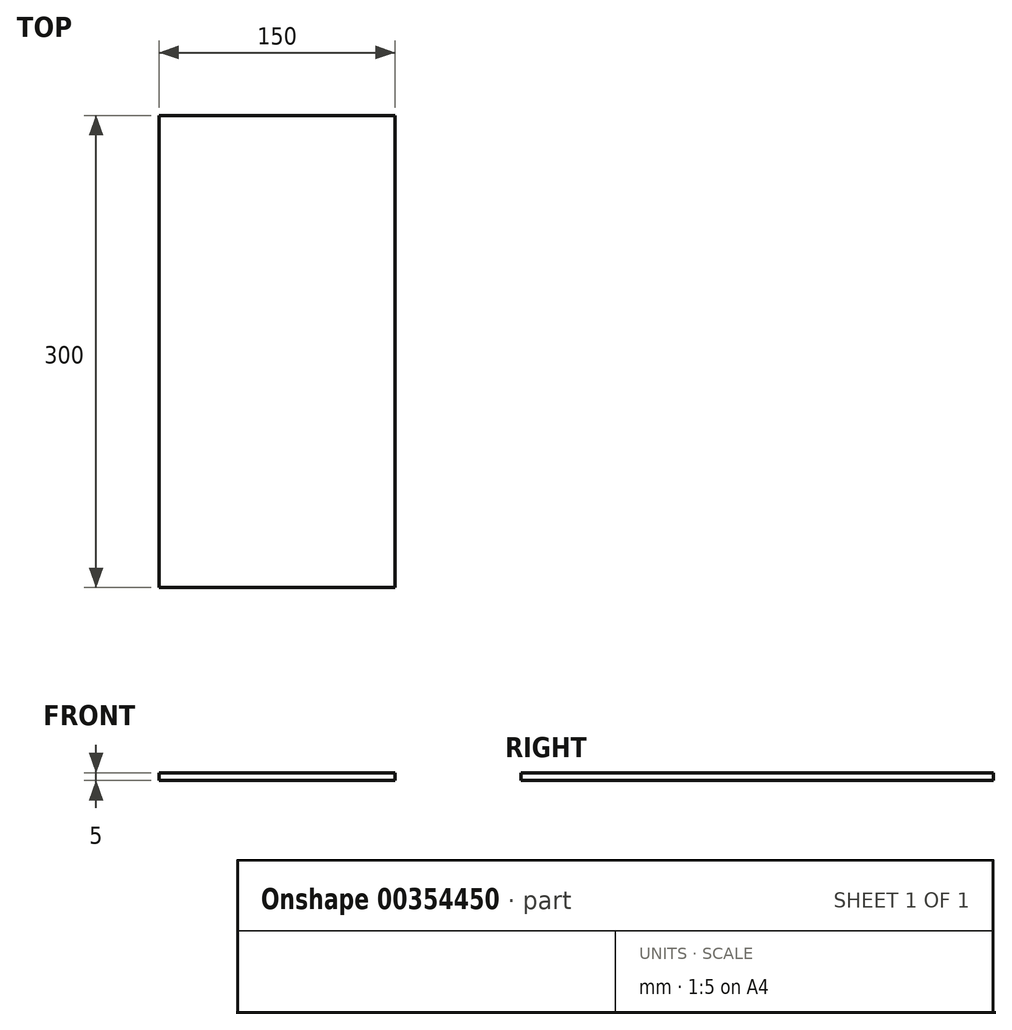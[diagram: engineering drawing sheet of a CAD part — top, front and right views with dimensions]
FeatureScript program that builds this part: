
annotation { "Feature Type Name" : "Feature", "Feature Type Description" : "" }
export const myFeature = defineFeature(function(context is Context, id is Id, definition is map)
    precondition{}
    {
        {
            var Q0;
            Q0=qCreatedBy(makeId("Top.planeOp"),FACE);
            var sketch = newSketch(context, id + "F0", { "sketchPlane" : qUnion([Q0])});
            skLineSegment(sketch, "E0.bottom", {"start": v(0, 0) * mm, "end": v(-150, 0) * mm});
            skLineSegment(sketch, "E0.top", {"start": v(0, 300) * mm, "end": v(-150, 300) * mm});
            skLineSegment(sketch, "E0.left", {"start": v(0, 0) * mm, "end": v(0, 300) * mm});
            skLineSegment(sketch, "E0.right", {"start": v(-150, 0) * mm, "end": v(-150, 300) * mm});
            skSolve(sketch);
        }
        {
            var Q0;
            Q0 = qSketchRegion(id + "F0", true);
            extrude(context, id + "F1", {"entities" : qUnion([Q0]), "depth" : 5 * mm});
        }
        {
            var Q0;
            Q0=qCreatedBy(makeId("Front.planeOp"),FACE);
            cPlane(context, id + "F2", {"entities" : qUnion([Q0]), "cplaneType" : CPlaneType.OFFSET, "offset" : 250 * mm, "oppositeDirection" : true, "width" : 150 * mm, "height" : 150 * mm});
        }
        {
            var Q0;
            Q0=qCreatedBy(makeId("Right.planeOp"),FACE);
            cPlane(context, id + "F3", {"entities" : qUnion([Q0]), "cplaneType" : CPlaneType.OFFSET, "offset" : 100 * mm, "oppositeDirection" : true, "width" : 150 * mm, "height" : 150 * mm});
        }
    });
